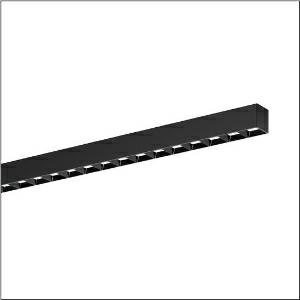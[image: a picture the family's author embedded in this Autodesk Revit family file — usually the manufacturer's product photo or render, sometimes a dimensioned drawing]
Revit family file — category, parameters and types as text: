
# Revit family: silica_21_51mx21tat4b
name_source: partatom
category: Lighting Fixtures
units: mm (PartAtom-declared; Revit-internal decimal feet)

## family parameters
Cut with Voids When Loaded = No
Host = Face
Light Source = No
Part Type = Normal
Room Calculation Point = No
Round Connector Dimension = Use Diameter
Shared = No

## types (1)
- --- (1 x LED, 3720 lm, 32.2 W, 6500K)
    Apparent Load = 32 VA
    CIE Flux Codes = 85 99 100 100 100
    Color Rendering = 80
    Color Temperature = 6500K
    Default Elevation = 1800 mm
    Description = Silica 21, office luminaire, primary light control with darklight reflector, of PMMA, black, CAT 2 (L<= 3000cd/m²), light emission: direct distribution, primary light characteristic: symmetric, installation type: surface-mounted, LED, rated luminous flux: 3.720lm, luminous efficacy: 110lm/W, light colour: 8tw, colour temperature: 2700..6500K, control gear: DALI DT8, with terminal, 3+2-pole, max. 2.5mm², mains connection: 220..240V, AC, 50/60Hz, rated input power: 33.8W, luminaire housing, of aluminium, matt jet black (RAL 9005), length: 1.204mm, width: 53mm, height: 53mm, protection rating (complete): IP20, insulation class (complete): insulation class I (protective earthing), certification: CE, permissible operating ambient temperature: 0..+35°C, standard: EN 50419, packaging unit: 1 piece
    Height = 53 mm
    Lamp = 1 x LED
    Lamp Light Flux = 3720 lm
    Lamp Power = 32.2 W
    Lamp count = 1
    Length = 1204 mm
    Luminous efficacy = 116 lm/W
    Manufacturer = Siteco
    ModVariant = No
    Model = 51MX21TAT4B
    Mounting Place = Ceiling
    Mounting Type = Surface mounted
    Number of Poles = 1
    OnlyDefault = Yes
    Power Factor = 1
    Product Name = Silica 21
    Product group = office luminaire | ceiling mounted
    ProductGroupID = 301
    Protection Class = Protection class I
    Protection Degree = IP 20
    RLX_Detail_Level = 1
    RLX_Emergency_Light_Flux = 0 lm
    RLX_Emergency_Type = 0
    RLX_Emergency_Type_DB = No
    RlxData = <blob elided: 40173 chars, md5=e6a6cf99>
    Socket = socket
    Standby Power = 0 W
    System Light Flux = 3720 lm
    System Power = 32 W
    Type Comments = individual setting
    Type Image = l_1335908.jpg
    URL = http://relux.com
    VarID = @adj_139565
    Voltage = 0 V
    Weight = 0.00 kg
    Width = 53 mm

## geometry (parser evidence)
native form markers: Blend x4, Sweep x9
no freeform markers — native parametric forms only
